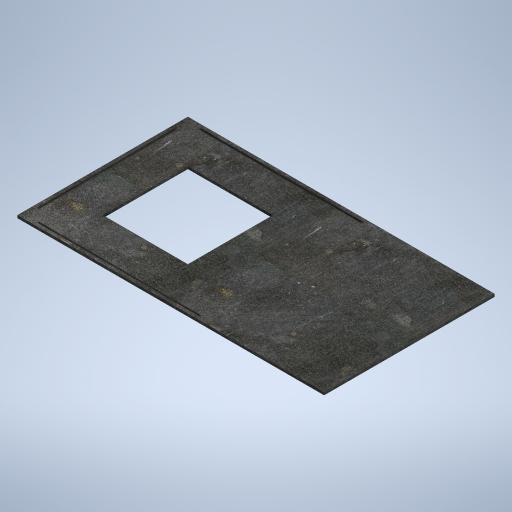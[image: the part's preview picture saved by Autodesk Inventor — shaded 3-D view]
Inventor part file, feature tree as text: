
AUTODESK INVENTOR PART (.ipt)
format: ipt  version: 2024.3 (Build 283343000, 343)  size: 372,736 bytes
history: native  units: mm
features: extrude x2, sketch x2
ambient origin geometry x8: Origin, YZ Plane, XZ Plane, XY Plane, X Axis, Y Axis, Z Axis, Center Point
bodies: Solid1 (feature_tree)
feature tree (4):
  extrude  "Extrusion1"  Depth=100.0mm
  extrude  "Extrusion3"  Depth=50.0mm
  sketch  "Sketch1"  dims[d0=100.0mm d1=100.0mm]
  sketch  "Sketch3"  dims[d2=200.0mm d3=50.0mm d4=210.0mm d5=0.0mm d6=200.0mm d7=3.0mm d8=0.0mm d13=2.0mm d14=2.0mm d15=4.0mm d16=4.0mm d17=4.0mm d18=2.0mm d19=150.0mm d20=2.0mm d21=15.0mm d22=15.0mm d23=15.0mm d24=15.0mm d25=10.0mm d26=0.0mm]
